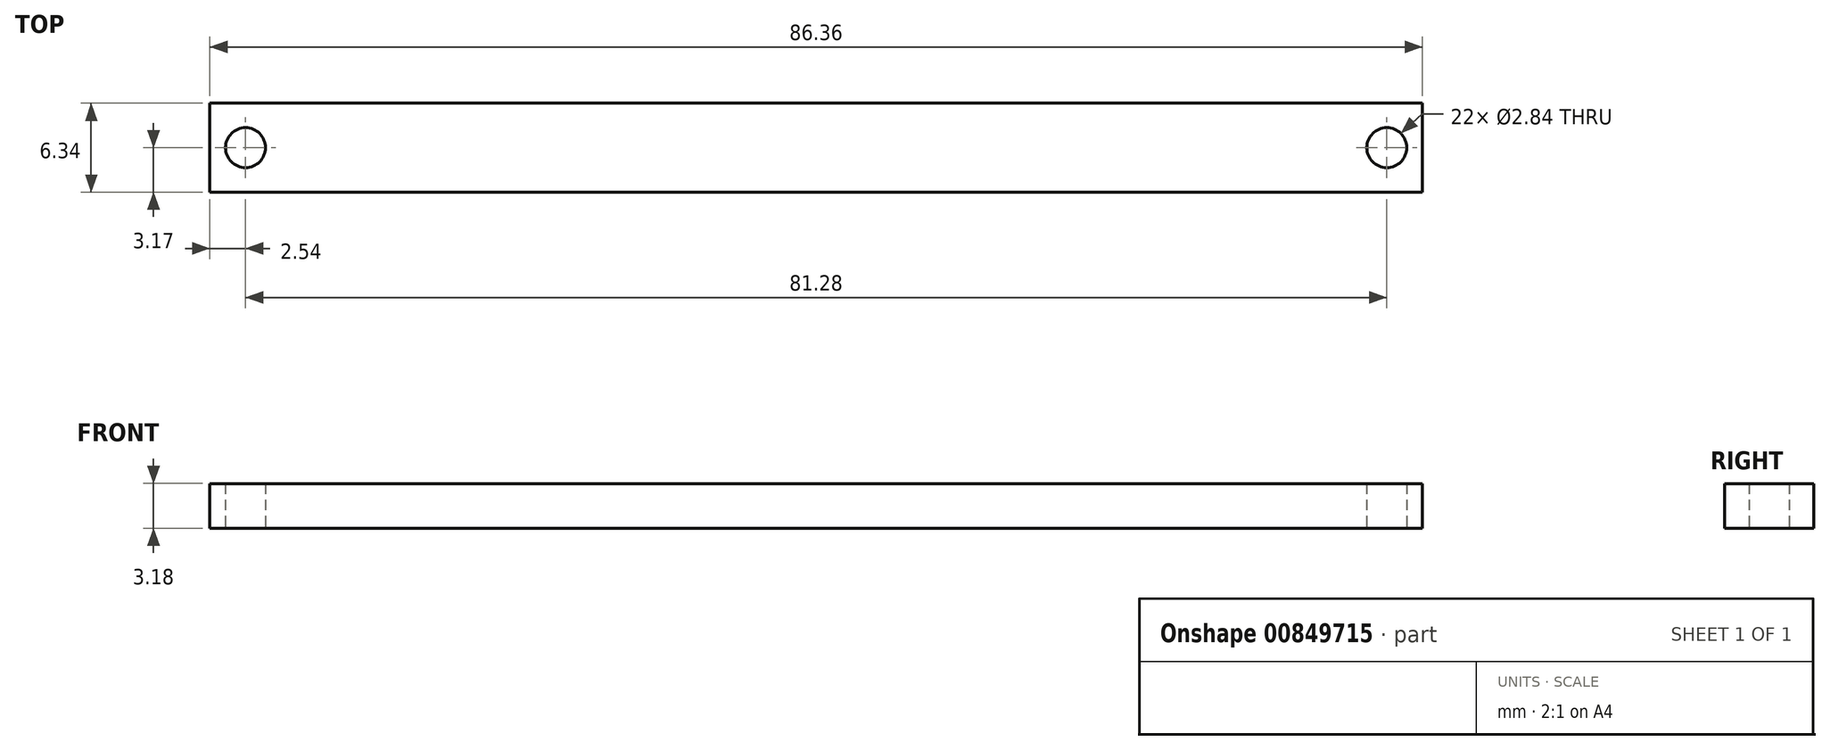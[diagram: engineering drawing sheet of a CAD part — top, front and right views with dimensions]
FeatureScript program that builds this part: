
annotation { "Feature Type Name" : "Feature", "Feature Type Description" : "" }
export const myFeature = defineFeature(function(context is Context, id is Id, definition is map)
    precondition{}
    {
        {
            var Q0;
            Q0=qCreatedBy(makeId("Top.planeOp"),FACE);
            var sketch = newSketch(context, id + "F0", { "sketchPlane" : qUnion([Q0])});
            skLineSegment(sketch, "E0.bottom", {"start": v(43.18, -3.17) * mm, "end": v(-43.18, -3.18) * mm});
            skLineSegment(sketch, "E0.top", {"start": v(43.18, 3.18) * mm, "end": v(-43.18, 3.17) * mm});
            skLineSegment(sketch, "E0.left", {"start": v(43.18, -3.17) * mm, "end": v(43.18, 3.18) * mm});
            skLineSegment(sketch, "E0.right", {"start": v(-43.18, -3.18) * mm, "end": v(-43.18, 3.17) * mm});
            skPoint(sketch, "E0.middle", {"position": v(0, 0) * mm});
            skCircle(sketch, "E1", {"center": v(-40.64, 0) * mm, "radius": 1.42 * mm});
            skCircle(sketch, "E2", {"center": v(40.64, 0) * mm, "radius": 1.42 * mm});
            skSolve(sketch);
        }
        {
            var Q0;
            Q0 = qSketchRegion(id + "F0", true);
            extrude(context, id + "F1", {"entities" : qUnion([Q0]), "depth" : 3.17 * mm, "offsetDistance" : 25.4 * mm});
        }
    });
